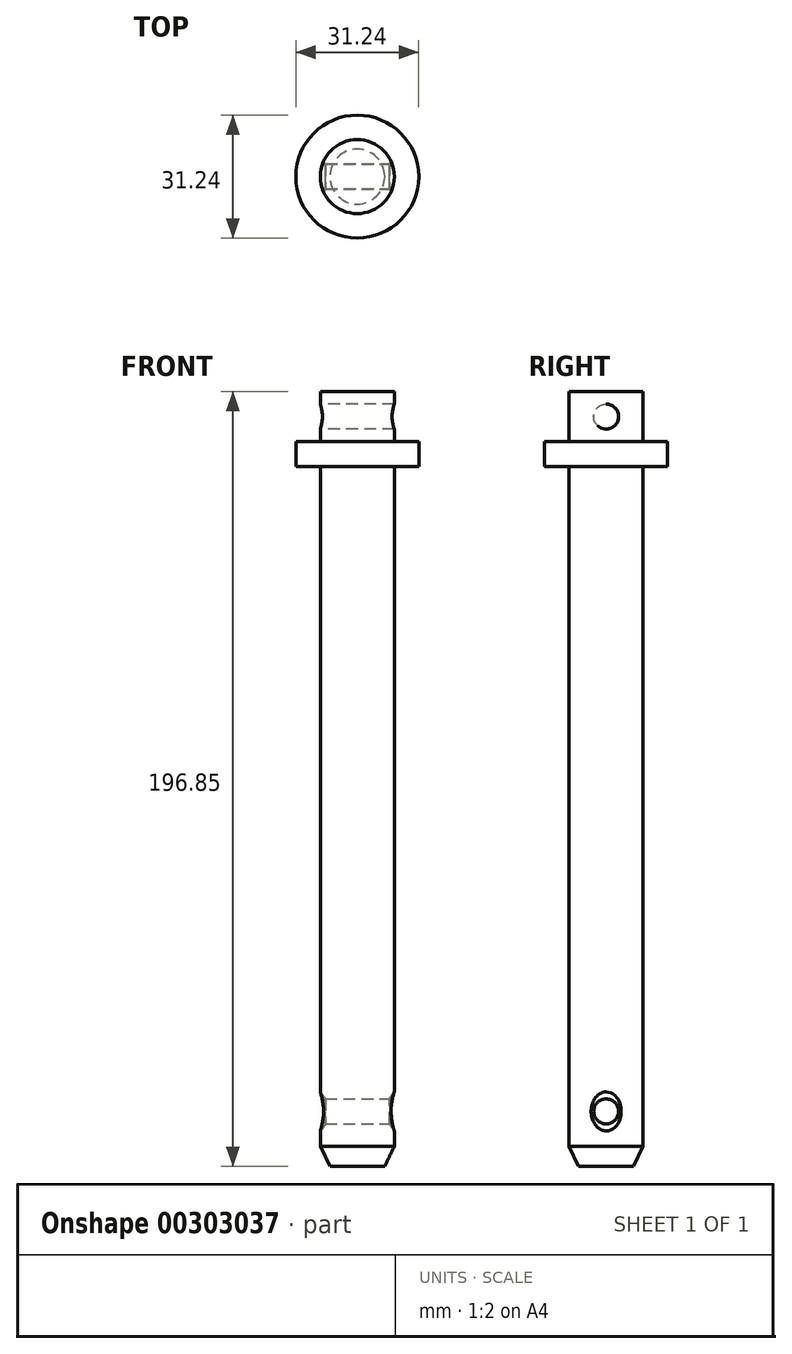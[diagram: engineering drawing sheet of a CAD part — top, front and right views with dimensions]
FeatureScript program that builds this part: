
annotation { "Feature Type Name" : "Feature", "Feature Type Description" : "" }
export const myFeature = defineFeature(function(context is Context, id is Id, definition is map)
    precondition{}
    {
        {
            var Q0;
            Q0=qCreatedBy(makeId("Front.planeOp"),FACE);
            var sketch = newSketch(context, id + "F0", { "sketchPlane" : qUnion([Q0])});
            skLineSegment(sketch, "E0", {"start": v(0, -88.9) * mm, "end": v(-6.99, -88.9) * mm});
            skLineSegment(sketch, "E1", {"start": v(-6.99, -88.9) * mm, "end": v(-9.4, -83.82) * mm});
            skLineSegment(sketch, "E2", {"start": v(-9.4, -83.82) * mm, "end": v(-9.4, 88.9) * mm});
            skLineSegment(sketch, "E3", {"start": v(-9.4, 88.9) * mm, "end": v(-15.62, 88.9) * mm});
            skLineSegment(sketch, "E4", {"start": v(-15.62, 88.9) * mm, "end": v(-15.62, 95.25) * mm});
            skLineSegment(sketch, "E5", {"start": v(-15.62, 95.25) * mm, "end": v(-9.4, 95.25) * mm});
            skLineSegment(sketch, "E6", {"start": v(-9.4, 95.25) * mm, "end": v(-9.4, 107.95) * mm});
            skLineSegment(sketch, "E7", {"start": v(-9.4, 107.95) * mm, "end": v(0, 107.95) * mm});
            skLineSegment(sketch, "E8.MirrorCS", {"start": v(0, -88.9) * mm, "end": v(6.99, -88.9) * mm});
            skLineSegment(sketch, "E9.MirrorCS", {"start": v(6.99, -88.9) * mm, "end": v(9.4, -83.82) * mm});
            skLineSegment(sketch, "E10.MirrorCS", {"start": v(9.4, -83.82) * mm, "end": v(9.4, 88.9) * mm});
            skLineSegment(sketch, "E11.MirrorCS", {"start": v(9.4, 88.9) * mm, "end": v(15.62, 88.9) * mm});
            skLineSegment(sketch, "E12.MirrorCS", {"start": v(15.62, 88.9) * mm, "end": v(15.62, 95.25) * mm});
            skLineSegment(sketch, "E13.MirrorCS", {"start": v(15.62, 95.25) * mm, "end": v(9.4, 95.25) * mm});
            skLineSegment(sketch, "E14.MirrorCS", {"start": v(9.4, 107.95) * mm, "end": v(0, 107.95) * mm});
            skLineSegment(sketch, "E15.MirrorCS", {"start": v(9.4, 95.25) * mm, "end": v(9.4, 107.95) * mm});
            skLineSegment(sketch, "E16", {"start": v(0, 118.74) * mm, "end": v(0, -113.6) * mm});
            skSolve(sketch);
        }
        {
            var Q0;
            {var subQ0=sQuery(id+"F0.wireOp",EDGE,"E0");Q0=makeQuery(id+"F0.imprint","IMPRINT",FACE,{"disambiguationData":[TD([[makeQuery(id+"F0.imprint","IMPRINT",EDGE,{"derivedFrom":subQ0}),-1.0]])]});}
            var Q1;
            Q1=sQuery(id+"F0.wireOp",EDGE,"E16");
            revolve(context, id + "F1", {"entities" : qUnion([Q0]), "axis" : qUnion([Q1]), "revolveType" : RevolveType.FULL});
        }
        {
            var Q0;
            Q0=qCreatedBy(makeId("Right.planeOp"),FACE);
            cPlane(context, id + "F2", {"entities" : qUnion([Q0]), "cplaneType" : CPlaneType.OFFSET, "offset" : 25.4 * mm, "width" : 152.4 * mm, "height" : 152.4 * mm});
        }
        {
            var Q0;
            Q0=qCreatedBy(id+"F2.planeOp",FACE);
            var sketch = newSketch(context, id + "F3", { "sketchPlane" : qUnion([Q0])});
            skPoint(sketch, "E17", {"position": v(0, 101.6) * mm});
            skPoint(sketch, "E18", {"position": v(0, -74.93) * mm});
            skSolve(sketch);
        }
        {
            var Q0;
            Q0=sQuery(id+"F3.wireOp",VERTEX,"E17");
            var Q1;
            Q1=makeQuery(id+"F1.opRevolve","SWEPT_BODY",BODY,{"disambiguationData":[OSD([sQuery(id+"F0.wireOp",EDGE,"E0"),sQuery(id+"F0.wireOp",EDGE,"E1"),sQuery(id+"F0.wireOp",EDGE,"E2"),sQuery(id+"F0.wireOp",EDGE,"E3"),sQuery(id+"F0.wireOp",EDGE,"E4"),sQuery(id+"F0.wireOp",EDGE,"E5"),sQuery(id+"F0.wireOp",EDGE,"E6"),sQuery(id+"F0.wireOp",EDGE,"E7"),sQuery(id+"F0.wireOp",EDGE,"E16")])]});
            hole(context, id + "F4", {"style" : HoleStyle.SIMPLE, "endStyle" : HoleEndStyle.THROUGH, "holeDiameter" : 6.35 * mm, "tappedDepth" : 12.7 * mm, "tapClearance" : 3, "locations" : qUnion([Q0]), "scope" : qUnion([Q1])});
        }
        {
            var Q0;
            Q0=qCreatedBy(makeId("Front.planeOp"),FACE);
            var sketch = newSketch(context, id + "F5", { "sketchPlane" : qUnion([Q0])});
            skLineSegment(sketch, "E19", {"start": v(-20.7, -74.93) * mm, "end": v(28.6, -74.93) * mm});
            skLineSegment(sketch, "E20", {"start": v(-8.13, -71.75) * mm, "end": v(8.13, -71.75) * mm});
            skLineSegment(sketch, "E21", {"start": v(8.13, -71.75) * mm, "end": v(10.23, -68.81) * mm});
            skLineSegment(sketch, "E22", {"start": v(10.23, -68.81) * mm, "end": v(10.23, -74.93) * mm});
            skLineSegment(sketch, "E23", {"start": v(10.23, -81.05) * mm, "end": v(8.13, -78.1) * mm});
            skLineSegment(sketch, "E24", {"start": v(8.13, -78.1) * mm, "end": v(-8.13, -78.1) * mm});
            skLineSegment(sketch, "E25", {"start": v(-8.13, -78.1) * mm, "end": v(-10.23, -81.05) * mm});
            skLineSegment(sketch, "E26", {"start": v(-10.23, -81.05) * mm, "end": v(-10.23, -74.93) * mm});
            skLineSegment(sketch, "E27", {"start": v(-10.23, -68.81) * mm, "end": v(-8.13, -71.75) * mm});
            skLineSegment(sketch, "E28", {"start": v(-10.23, -74.93) * mm, "end": v(-10.23, -68.81) * mm});
            skLineSegment(sketch, "E29", {"start": v(10.23, -74.93) * mm, "end": v(10.23, -81.05) * mm});
            skLineSegment(sketch, "E30", {"start": v(-9.4, -83.82) * mm, "end": v(-9.4, 88.9) * mm});
            skLineSegment(sketch, "E31", {"start": v(9.4, 88.9) * mm, "end": v(9.4, -83.82) * mm});
            skPoint(sketch, "E32", {"position": v(9.4, -69.98) * mm});
            skPoint(sketch, "E33", {"position": v(9.4, -79.88) * mm});
            skSolve(sketch);
        }
        {
            var Q0;
            Q0=makeQuery(id+"F5.imprint","IMPRINT",FACE,{"disambiguationData":[TD([[makeQuery(id+"F5.imprint","IMPRINT",EDGE,{"derivedFrom":sQuery(id+"F5.wireOp",EDGE,"E20")}),-1.0]])]});
            var Q1;
            Q1=sQuery(id+"F5.wireOp",EDGE,"E19");
            revolve(context, id + "F6", {"operationType" : NewBodyOperationType.REMOVE, "entities" : qUnion([Q0]), "axis" : qUnion([Q1]), "revolveType" : RevolveType.FULL, "oppositeDirection" : true});
        }
    });
